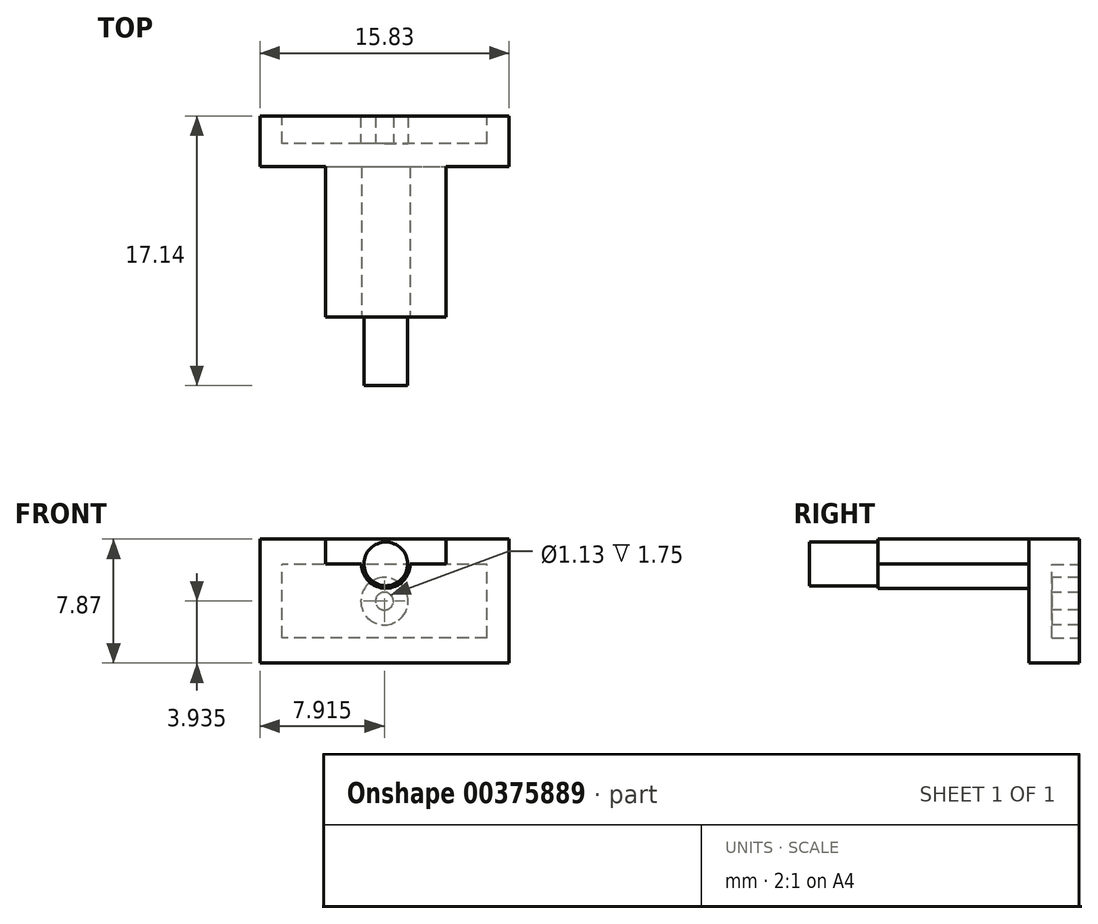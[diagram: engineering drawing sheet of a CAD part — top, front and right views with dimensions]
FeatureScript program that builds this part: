
annotation { "Feature Type Name" : "Feature", "Feature Type Description" : "" }
export const myFeature = defineFeature(function(context is Context, id is Id, definition is map)
    precondition{}
    {
        {
            var Q0;
            Q0=qCreatedBy(makeId("Front.planeOp"),FACE);
            var sketch = newSketch(context, id + "F0", { "sketchPlane" : qUnion([Q0])});
            skLineSegment(sketch, "E0.bottom", {"start": v(0, 0) * mm, "end": v(15.83, 0) * mm});
            skLineSegment(sketch, "E0.top", {"start": v(0, 7.87) * mm, "end": v(15.83, 7.87) * mm});
            skLineSegment(sketch, "E0.left", {"start": v(0, 0) * mm, "end": v(0, 7.87) * mm});
            skLineSegment(sketch, "E0.right", {"start": v(15.83, 0) * mm, "end": v(15.83, 7.87) * mm});
            skSolve(sketch);
        }
        {
            var Q0;
            Q0 = qSketchRegion(id + "F0", true);
            extrude(context, id + "F1", {"entities" : qUnion([Q0]), "depth" : 3.2 * mm});
        }
        {
            var Q0;
            Q0=makeQuery(id+"F1.opExtrude","CAP_FACE",FACE,{"disambiguationData":[OSD([sQuery(id+"F0.wireOp",EDGE,"E0.bottom"),sQuery(id+"F0.wireOp",EDGE,"E0.top"),sQuery(id+"F0.wireOp",EDGE,"E0.left"),sQuery(id+"F0.wireOp",EDGE,"E0.right")])],"isStart":true});
            var sketch = newSketch(context, id + "F2", { "sketchPlane" : qUnion([Q0])});
            skLineSegment(sketch, "E1.bottom", {"start": v(-14.43, 1.6) * mm, "end": v(-1.4, 1.6) * mm});
            skLineSegment(sketch, "E1.top", {"start": v(-14.43, 6.27) * mm, "end": v(-1.4, 6.27) * mm});
            skLineSegment(sketch, "E1.left", {"start": v(-14.43, 1.6) * mm, "end": v(-14.43, 6.27) * mm});
            skLineSegment(sketch, "E1.right", {"start": v(-1.4, 1.6) * mm, "end": v(-1.4, 6.27) * mm});
            skSolve(sketch);
        }
        {
            var Q0;
            Q0 = qSketchRegion(id + "F2", true);
            extrude(context, id + "F3", {"entities" : qUnion([Q0]), "operationType" : NewBodyOperationType.REMOVE, "oppositeDirection" : true, "depth" : 1.75 * mm});
        }
        {
            var Q0;
            Q0=makeQuery(id+"F3.boolean.opBoolean","COPY",FACE,{"derivedFrom":makeQuery(id+"F3.opExtrude","CAP_FACE",FACE,{"disambiguationData":[OSD([sQuery(id+"F2.wireOp",EDGE,"E1.bottom"),sQuery(id+"F2.wireOp",EDGE,"E1.top"),sQuery(id+"F2.wireOp",EDGE,"E1.left"),sQuery(id+"F2.wireOp",EDGE,"E1.right")])],"isStart":false})});
            var sketch = newSketch(context, id + "F4", { "sketchPlane" : qUnion([Q0])});
            skCircle(sketch, "E2", {"center": v(-7.92, 3.93) * mm, "radius": 1.5 * mm});
            skPoint(sketch, "E2.centerSnap0", {"position": v(-1.4, 3.93) * mm});
            skPoint(sketch, "E2.centerSnap1", {"position": v(-7.92, 6.27) * mm});
            skCircle(sketch, "E3", {"center": v(-7.92, 3.93) * mm, "radius": 0.56 * mm});
            skSolve(sketch);
        }
        {
            var Q0;
            Q0 = qSketchRegion(id + "F4", true);
            var Q1;
            Q1=makeQuery(id+"F1.opExtrude","CAP_FACE",FACE,{"disambiguationData":[OSD([sQuery(id+"F0.wireOp",EDGE,"E0.bottom"),sQuery(id+"F0.wireOp",EDGE,"E0.top"),sQuery(id+"F0.wireOp",EDGE,"E0.left"),sQuery(id+"F0.wireOp",EDGE,"E0.right")])],"isStart":true});
            extrude(context, id + "F5", {"entities" : qUnion([Q0]), "operationType" : NewBodyOperationType.ADD, "endBound" : BoundingType.UP_TO_SURFACE, "endBoundEntityFace" : qUnion([Q1]), "depth" : 2 * mm});
        }
        {
            var Q0;
            Q0=makeQuery(id+"F1.opExtrude","CAP_FACE",FACE,{"disambiguationData":[OSD([sQuery(id+"F0.wireOp",EDGE,"E0.bottom"),sQuery(id+"F0.wireOp",EDGE,"E0.top"),sQuery(id+"F0.wireOp",EDGE,"E0.left"),sQuery(id+"F0.wireOp",EDGE,"E0.right")])],"isStart":false});
            var sketch = newSketch(context, id + "F6", { "sketchPlane" : qUnion([Q0])});
            skLineSegment(sketch, "E4.bottom", {"start": v(4.17, 7.87) * mm, "end": v(11.83, 7.87) * mm});
            skLineSegment(sketch, "E4.top", {"start": v(4.17, 6.3) * mm, "end": v(11.83, 6.3) * mm});
            skLineSegment(sketch, "E4.left", {"start": v(4.17, 7.87) * mm, "end": v(4.17, 6.3) * mm});
            skLineSegment(sketch, "E4.right", {"start": v(11.83, 7.87) * mm, "end": v(11.83, 6.3) * mm});
            skSolve(sketch);
        }
        {
            var Q0;
            Q0 = qSketchRegion(id + "F6", true);
            extrude(context, id + "F7", {"entities" : qUnion([Q0]), "operationType" : NewBodyOperationType.ADD, "depth" : 9.58 * mm});
        }
        {
            var Q0;
            Q0=makeQuery(id+"F7.opExtrude","CAP_FACE",FACE,{"disambiguationData":[OSD([sQuery(id+"F6.wireOp",EDGE,"E4.bottom"),sQuery(id+"F6.wireOp",EDGE,"E4.top"),sQuery(id+"F6.wireOp",EDGE,"E4.left"),sQuery(id+"F6.wireOp",EDGE,"E4.right")])],"isStart":false});
            var sketch = newSketch(context, id + "F8", { "sketchPlane" : qUnion([Q0])});
            skCircle(sketch, "E5", {"center": v(8, 6.3) * mm, "radius": 1.55 * mm});
            skSolve(sketch);
        }
        {
            var Q0;
            Q0 = qSketchRegion(id + "F8", true);
            var Q1;
            Q1=makeQuery(id+"F1.opExtrude","CAP_FACE",FACE,{"disambiguationData":[OSD([sQuery(id+"F0.wireOp",EDGE,"E0.bottom"),sQuery(id+"F0.wireOp",EDGE,"E0.top"),sQuery(id+"F0.wireOp",EDGE,"E0.left"),sQuery(id+"F0.wireOp",EDGE,"E0.right")])],"isStart":false});
            extrude(context, id + "F9", {"entities" : qUnion([Q0]), "operationType" : NewBodyOperationType.ADD, "endBound" : BoundingType.UP_TO_SURFACE, "oppositeDirection" : true, "endBoundEntityFace" : qUnion([Q1]), "depth" : 25 * mm});
        }
        {
            var Q0;
            Q0=makeQuery(id+"F9.boolean.opBoolean","MERGE",FACE,{"derivedFrom":[makeQuery(id+"F7.opExtrude","CAP_FACE",FACE,{"disambiguationData":[OSD([sQuery(id+"F6.wireOp",EDGE,"E4.bottom"),sQuery(id+"F6.wireOp",EDGE,"E4.top"),sQuery(id+"F6.wireOp",EDGE,"E4.left"),sQuery(id+"F6.wireOp",EDGE,"E4.right")])],"isStart":false}),makeQuery(id+"F9.opExtrude","CAP_FACE",FACE,{"disambiguationData":[OSD([sQuery(id+"F8.wireOp",EDGE,"E5")])],"isStart":true})]});
            var sketch = newSketch(context, id + "F10", { "sketchPlane" : qUnion([Q0])});
            skCircle(sketch, "E6", {"center": v(8, 6.3) * mm, "radius": 1.39 * mm});
            skSolve(sketch);
        }
        {
            var Q0;
            Q0 = qSketchRegion(id + "F10", true);
            extrude(context, id + "F11", {"entities" : qUnion([Q0]), "operationType" : NewBodyOperationType.ADD, "depth" : 4.35 * mm});
        }
    });
